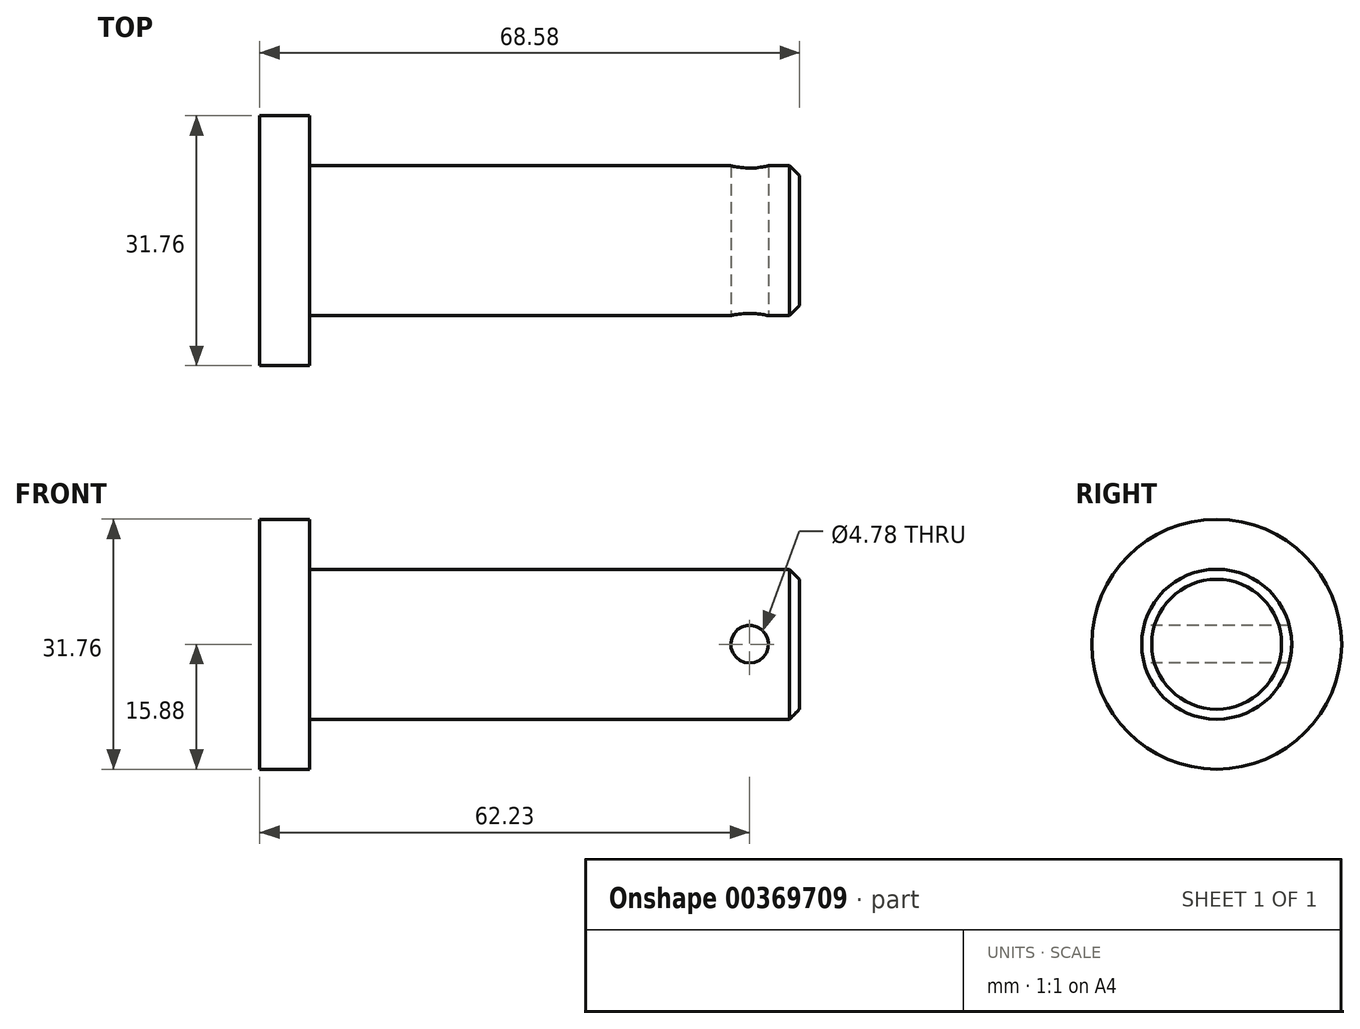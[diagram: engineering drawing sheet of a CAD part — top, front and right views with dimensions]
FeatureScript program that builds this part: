
annotation { "Feature Type Name" : "Feature", "Feature Type Description" : "" }
export const myFeature = defineFeature(function(context is Context, id is Id, definition is map)
    precondition{}
    {
        {
            var Q0;
            Q0=qCreatedBy(makeId("Right.planeOp"),FACE);
            var sketch = newSketch(context, id + "F0", { "sketchPlane" : qUnion([Q0])});
            skCircle(sketch, "E0", {"center": v(0, 0) * mm, "radius": 15.88 * mm});
            skSolve(sketch);
        }
        {
            var Q0;
            Q0=makeQuery(id+"F0.imprint","IMPRINT",FACE,{"disambiguationData":[TD([[makeQuery(id+"F0.imprint","IMPRINT",EDGE,{"derivedFrom":sQuery(id+"F0.wireOp",EDGE,"E0")}),1.0]])]});
            extrude(context, id + "F1", {"entities" : qUnion([Q0]), "depth" : 6.35 * mm});
        }
        {
            var Q0;
            Q0=makeQuery(id+"F1.opExtrude","CAP_FACE",FACE,{"disambiguationData":[OSD([sQuery(id+"F0.wireOp",EDGE,"E0")])],"isStart":false});
            var sketch = newSketch(context, id + "F2", { "sketchPlane" : qUnion([Q0])});
            skCircle(sketch, "E1", {"center": v(0, 0) * mm, "radius": 9.53 * mm});
            skSolve(sketch);
        }
        {
            var Q0;
            Q0=makeQuery(id+"F2.imprint","IMPRINT",FACE,{"disambiguationData":[TD([[makeQuery(id+"F2.imprint","IMPRINT",EDGE,{"derivedFrom":sQuery(id+"F2.wireOp",EDGE,"E1")}),1.0]])]});
            extrude(context, id + "F3", {"entities" : qUnion([Q0]), "operationType" : NewBodyOperationType.ADD, "depth" : 62.23 * mm});
        }
        {
            var Q0;
            Q0=makeQuery(id+"F3.opExtrude","CAP_EDGE",EDGE,{"disambiguationData":[OSD([sQuery(id+"F2.wireOp",EDGE,"E1")])],"isStart":false});
            chamfer(context, id + "F4", {"entities" : qUnion([Q0]), "width" : 1.27 * mm, "tangentPropagation" : true});
        }
        {
            var Q0;
            Q0=qCreatedBy(makeId("Front.planeOp"),FACE);
            var sketch = newSketch(context, id + "F5", { "sketchPlane" : qUnion([Q0])});
            skLineSegment(sketch, "E2", {"start": v(0, 0) * mm, "end": v(62.23, 0) * mm, "construction": true});
            skCircle(sketch, "E3", {"center": v(62.23, 0) * mm, "radius": 2.39 * mm});
            skSolve(sketch);
        }
        {
            var Q0;
            Q0 = qSketchRegion(id + "F5", true);
            extrude(context, id + "F6", {"entities" : qUnion([Q0]), "operationType" : NewBodyOperationType.REMOVE, "oppositeDirection" : true, "depth" : 25.4 * mm, "hasSecondDirection" : true, "secondDirectionOppositeDirection" : false, "secondDirectionDepth" : 25.4 * mm});
        }
    });
